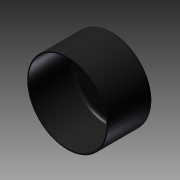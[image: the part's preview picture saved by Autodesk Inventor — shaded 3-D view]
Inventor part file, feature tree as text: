
AUTODESK INVENTOR PART (.ipt)
format: ipt  version: 2011 (Build 150239000, 239)  size: 102,912 bytes
history: native  units: in
note: dims shown in document units (in); Inventor stores cm internally (conversion verified against a paired STEP export)
features: extrude x2, sketch x2, fillet x1
ambient origin geometry x8: Origin, YZ Plane, XZ Plane, XY Plane, X Axis, Y Axis, Z Axis, Center Point
bodies: Solid1 (feature_tree)
feature tree (5):
  extrude  "Extrusion1"  Depth=1.55in
  extrude  "Extrusion2"  Depth=0.05in TaperAngle=0.0deg
  fillet  "Fillet1"  Radius=0.0625in
  sketch  "Sketch1"  dims[d0=1.6in d1=1.55in]
  sketch  "Sketch2"  dims[d2=0.85in d3=0.0in d4=0.05in d5=0.0in d6=0.0625in]
